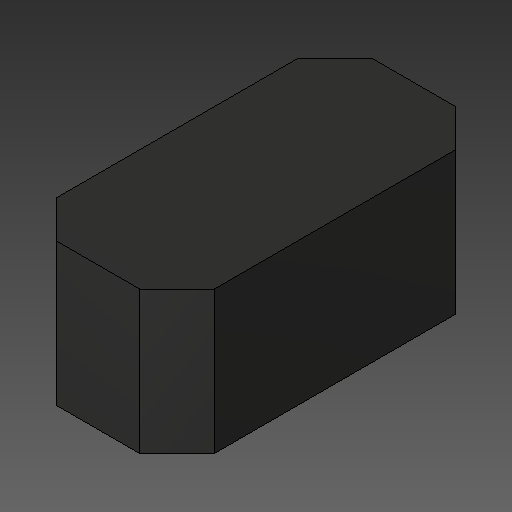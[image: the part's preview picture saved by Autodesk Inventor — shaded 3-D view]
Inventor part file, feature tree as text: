
AUTODESK INVENTOR PART (.ipt)
format: ipt  version: 2018.2 (Build 222227000, 227)  size: 85,504 bytes
history: native  units: mm
features: other x1, chamfer x1
ambient origin geometry x8: Origin, YZ Plane, XZ Plane, XY Plane, X Axis, Y Axis, Z Axis, Center Point
bodies: Body1 (feature_tree)
feature tree (2):
  other  "ソリッド1"
  chamfer  "Chamfer1"  [1 undecoded]
note: 1 required parameter value undecoded (feature->parameter linkage not recoverable at this tier; creation-order binding heuristic only, values carry confidence <= 0.55)
